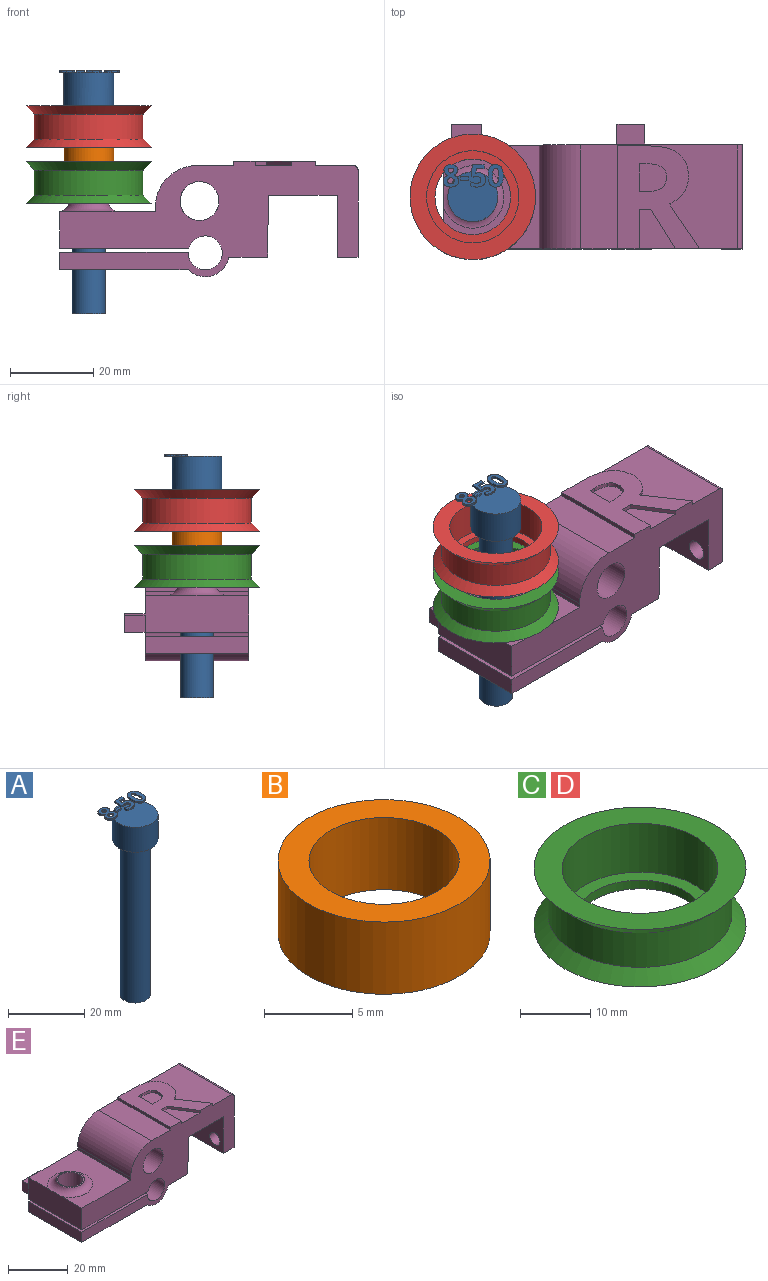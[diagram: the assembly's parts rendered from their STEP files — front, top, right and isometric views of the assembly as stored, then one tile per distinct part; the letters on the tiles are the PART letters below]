
ASSEMBLY  parts=5 mates=4
PART A: 86 faces, bbox 14.5x13.7x58.5 mm
  f0: plane 12x12mm, normal (0,0,1), area 99.4mm2, adj f5,f22,f23,f24,f25,f26,f40,f41
  f1: plane 1x0.26mm, normal (0,0,1), area 0.1mm2, adj f5,f46,f47,f48,f49
  f2: plane 0.85x0.68mm, normal (0,0,1), area 0.2mm2, adj f5,f29,f30,f31
  f3: cylinder r=4mm len=50mm, axis (0,0,-1), area 1256.6mm2, adj f4,f6
  f4: plane 8x8mm, normal (0,0,-1), area 50.3mm2, adj f3
  f5: cylinder r=6mm len=12mm, axis (0,0,-1), area 301.6mm2, adj f0,f1,f2,f6,f39,f45,f67,f85
  f6: plane 12x12mm, normal (0,0,-1), area 62.8mm2, adj f3,f5
  f7: extruded ~0.5x0.46mm, area 0.2mm2, adj f8,f37,f38,f39
  f8: extruded ~0.5x0.46mm, area 0.2mm2, adj f7,f9,f38,f39
  f9: extruded ~0.5x0.39mm, area 0.2mm2, adj f8,f10,f38,f39
  f10: extruded ~0.5x0.4mm, area 0.2mm2, adj f9,f11,f38,f39
  f11: extruded ~0.5x0.49mm, area 0.3mm2, adj f10,f12,f38,f39
  f12: extruded ~0.5x0.5mm, area 0.3mm2, adj f11,f13,f38,f39
  f13: extruded ~0.5x0.39mm, area 0.2mm2, adj f12,f37,f38,f39
  f14: extruded ~1.22x0.5mm, area 0.6mm2, adj f15,f35,f38,f39
  f15: extruded ~1.22x0.5mm, area 0.6mm2, adj f14,f16,f38,f39
  f16: extruded ~0.91x0.5mm, area 0.5mm2, adj f15,f17,f38,f39
  f17: extruded ~0.71x0.5mm, area 0.4mm2, adj f16,f18,f38,f39
  f18: extruded ~0.65x0.61mm, area 0.4mm2, adj f17,f19,f38,f39
  f19: extruded ~0.77x0.62mm, area 0.5mm2, adj f18,f20,f38,f39
  f20: extruded ~0.8x0.5mm, area 0.4mm2, adj f19,f21,f38,f39
  f21: extruded ~1.04x0.5mm, area 0.6mm2, adj f20,f22,f38,f39
  f22: extruded ~1.36x0.5mm, area 0.7mm2, adj f0,f21,f23,f38,f39
  f23: extruded ~1.33x0.5mm, area 0.7mm2, adj f0,f22,f24,f38
  f24: extruded ~1.04x0.51mm, area 0.6mm2, adj f0,f23,f25,f38
  f25: extruded ~0.75x0.5mm, area 0.4mm2, adj f0,f24,f26,f38
  f26: extruded ~0.85x0.66mm, area 0.5mm2, adj f0,f25,f27,f38,f39
  f27: extruded ~0.72x0.56mm, area 0.5mm2, adj f26,f28,f38,f39
  f28: extruded ~0.72x0.5mm, area 0.4mm2, adj f27,f35,f38,f39
  f29: extruded ~0.5x0.45mm, area 0.3mm2, adj f2,f30,f36,f38,f39
  f30: extruded ~0.5x0.47mm, area 0.3mm2, adj f2,f29,f31,f38
  f31: extruded ~0.62x0.5mm, area 0.3mm2, adj f2,f30,f32,f38,f39
  f32: extruded ~0.59x0.5mm, area 0.3mm2, adj f31,f33,f38,f39
  f33: extruded ~0.5x0.48mm, area 0.3mm2, adj f32,f34,f38,f39
  f34: extruded ~0.89x0.77mm, area 0.6mm2, adj f33,f36,f38,f39
  f35: extruded ~0.93x0.5mm, area 0.5mm2, adj f14,f28,f38,f39
  f36: extruded ~0.66x0.5mm, area 0.4mm2, adj f29,f34,f38,f39
  f37: extruded ~0.5x0.39mm, area 0.2mm2, adj f7,f13,f38,f39
  f38: plane 5.4x3.69mm, normal (0,0,1), area 12.7mm2, adj f7,f8,f9,f10,f11,f12,f13,f14
  f39: plane 5.4x3.53mm, normal (0,0,-1), area 10.2mm2, adj f5,f7,f8,f9,f10,f11,f12,f13
  f40: plane 0.9x0.5mm, normal (-1,0,0), area 0.4mm2, adj f0,f41,f43,f44
  f41: plane 1.93x0.5mm, normal (0,-1,0), area 1mm2, adj f0,f40,f42,f44
  f42: plane 0.9x0.5mm, normal (1,0,0), area 0.4mm2, adj f0,f41,f43,f44
  f43: plane 1.93x0.5mm, normal (0,1,0), area 1mm2, adj f0,f40,f42,f44
  f44: plane 1.93x0.9mm, normal (0,0,1), area 1.7mm2, adj f40,f41,f42,f43
  f45: plane 0.76x0.31mm, normal (0,0,-1), area 0mm2, adj f5,f46
  f46: extruded ~1.21x0.5mm, area 0.7mm2, adj f0,f1,f45,f47,f65,f66
  f47: extruded ~0.54x0.5mm, area 0.3mm2, adj f1,f46,f48,f66
  f48: plane 0.5x0.13mm, normal (-0.2,0.98,0), area 0.1mm2, adj f1,f47,f49,f66
  f49: plane 1.03x0.5mm, normal (1,-0.09,0), area 0.5mm2, adj f1,f48,f50,f66,f67
  f50: plane 1.88x0.5mm, normal (0,-1,0), area 0.9mm2, adj f49,f51,f66,f67
  f51: plane 0.94x0.5mm, normal (1,0,0), area 0.5mm2, adj f50,f52,f66,f67
  f52: plane 2.85x0.5mm, normal (0,1,0), area 1.4mm2, adj f51,f53,f66,f67
  f53: plane 2.68x0.5mm, normal (-1,0.07,0), area 1.3mm2, adj f0,f52,f54,f66,f67
  f54: plane 0.5x0.44mm, normal (-0.47,-0.88,0), area 0.3mm2, adj f0,f53,f55,f66
  f55: extruded ~0.5x0.37mm, area 0.2mm2, adj f0,f54,f56,f66
  f56: extruded ~0.5x0.42mm, area 0.2mm2, adj f0,f55,f57,f66
  f57: extruded ~1.05x0.8mm, area 0.8mm2, adj f0,f56,f58,f66
  f58: extruded ~1.02x0.83mm, area 0.8mm2, adj f0,f57,f59,f66
  f59: extruded ~0.72x0.5mm, area 0.4mm2, adj f0,f58,f60,f66
  f60: extruded ~0.66x0.5mm, area 0.4mm2, adj f0,f59,f61,f66
  f61: plane 0.96x0.5mm, normal (-1,0,0), area 0.5mm2, adj f0,f60,f62,f66
  f62: extruded ~1.42x0.5mm, area 0.7mm2, adj f0,f61,f63,f66
  f63: extruded ~1.55x0.5mm, area 0.8mm2, adj f0,f62,f64,f66
  f64: extruded ~1.36x0.54mm, area 0.8mm2, adj f0,f63,f65,f66
  f65: extruded ~1.17x0.5mm, area 0.6mm2, adj f0,f46,f64,f66
  f66: plane 5.33x3.51mm, normal (0,0,1), area 10.9mm2, adj f46,f47,f48,f49,f50,f51,f52,f53
  f67: plane 2.97x1.71mm, normal (0,0,-1), area 3.5mm2, adj f5,f49,f50,f51,f52,f53
  f68: extruded ~1.39x0.5mm, area 0.7mm2, adj f69,f83,f84,f85
  f69: extruded ~1.39x0.5mm, area 0.7mm2, adj f68,f70,f84,f85
  f70: extruded ~0.56x0.5mm, area 0.4mm2, adj f69,f71,f84,f85
  f71: extruded ~0.56x0.5mm, area 0.4mm2, adj f70,f72,f84,f85
  f72: extruded ~1.39x0.5mm, area 0.7mm2, adj f71,f73,f84,f85
  f73: extruded ~1.38x0.5mm, area 0.7mm2, adj f72,f74,f84,f85
  f74: extruded ~0.56x0.5mm, area 0.4mm2, adj f73,f83,f84,f85
  f75: extruded ~2.04x0.5mm, area 1.1mm2, adj f76,f82,f84,f85
  f76: extruded ~2.02x0.5mm, area 1.1mm2, adj f75,f77,f84,f85
  f77: extruded ~1.38x0.69mm, area 0.8mm2, adj f76,f78,f84,f85
  f78: extruded ~1.38x0.66mm, area 0.8mm2, adj f77,f79,f84,f85
  f79: extruded ~2.05x0.5mm, area 1.1mm2, adj f78,f80,f84,f85
  f80: extruded ~2.02x0.5mm, area 1mm2, adj f0,f79,f81,f84,f85
  f81: extruded ~1.37x0.68mm, area 0.8mm2, adj f0,f80,f82,f84
  f82: extruded ~1.39x0.66mm, area 0.8mm2, adj f0,f75,f81,f84,f85
  f83: extruded ~0.56x0.5mm, area 0.4mm2, adj f68,f74,f84,f85
  f84: plane 5.41x3.68mm, normal (0,0,1), area 12.1mm2, adj f68,f69,f70,f71,f72,f73,f74,f75
  f85: plane 5.41x3.68mm, normal (0,0,-1), area 10.3mm2, adj f5,f68,f69,f70,f71,f72,f73,f74
PART B: 4 faces, bbox 12x12x5 mm
  f0: cylinder r=4.25mm len=8.5mm, axis (0,0,-1), area 133.5mm2, adj f2,f3
  f1: cylinder r=6mm len=12mm, axis (0,0,-1), area 188.5mm2, adj f2,f3
  f2: plane 12x12mm, normal (0,0,1), area 56.4mm2, adj f0,f1
  f3: plane 12x12mm, normal (0,0,-1), area 56.4mm2, adj f0,f1
PART C: 8 faces, bbox 30.2x30.2x10 mm
  f0: plane 30.2x30.2mm, normal (0,0,1), area 329.2mm2, adj f1,f7
  f1: cylinder r=11.1mm len=22.2mm, axis (0,0,-1), area 592.8mm2, adj f0,f2
  f2: plane 22.2x22.2mm, normal (0,0,1), area 126.9mm2, adj f1,f3
  f3: cylinder r=9.1mm len=18.2mm, axis (0,0,-1), area 85.8mm2, adj f2,f4
  f4: plane 30.2x30.2mm, normal (0,0,-1), area 456.2mm2, adj f3,f5
  f5: cone r=13.1mm half-angle=45deg, axis (0,0,-1), area 250.6mm2, adj f4,f6
  f6: cylinder r=13.1mm len=26.2mm, axis (0,0,-1), area 493.9mm2, adj f5,f7
  f7: cone r=15.1mm half-angle=45deg, axis (0,0,1), area 250.6mm2, adj f0,f6
PART D: same geometry as C
PART E: 56 faces, bbox 75.2x30x27.7 mm
  f0: plane 37.77x25mm, normal (0,0,1), area 550.8mm2, adj f14,f15,f25,f27,f40,f41,f42,f43
  f1: plane 9.51x8.71mm, normal (0,0,1), area 54.7mm2, adj f14,f37,f38,f39
  f2: plane 25x4.12mm, normal (-1,0,0), area 103mm2, adj f5,f14,f15,f19
  f3: cylinder r=4.17mm len=8.35mm, axis (0,0,1), area 108.1mm2, adj f5,f19
  f4: plane 25x9.34mm, normal (0,0,-1), area 233.4mm2, adj f13,f14,f15,f17
  f5: plane 30.88x25mm, normal (0,0,-1), area 717.2mm2, adj f2,f3,f14,f15,f17
  f6: plane 25x8.82mm, normal (-1,0,0), area 219.6mm2, adj f7,f14,f15,f20,f24
  f7: plane 25x23mm, normal (0,0,1), area 400mm2, adj f6,f8,f14,f15,f24
  f8: plane 25x1.1mm, normal (-1,0,0), area 27.5mm2, adj f7,f14,f15,f25
  f9: plane 25x21.09mm, normal (1,0,0), area 493.5mm2, adj f10,f14,f15,f22,f23,f27
  f10: plane 25x5mm, normal (0,0,-1), area 125mm2, adj f9,f11,f14,f15
  f11: plane 25x15mm, normal (-1,0,0), area 341.3mm2, adj f10,f12,f14,f15,f22,f23
  f12: plane 25x16.55mm, normal (0,0,-1), area 413.8mm2, adj f11,f13,f14,f15
  f13: plane 25x14.91mm, normal (1,0,-0.01), area 372.8mm2, adj f4,f12,f14,f15
  f14: plane 71.77x27.75mm, normal (0,-1,0), area 1042.9mm2, adj f0,f1,f2,f4,f5,f6,f7,f8
  f15: plane 71.77x26.75mm, normal (0,1,0), area 971.8mm2, adj f0,f2,f4,f5,f6,f7,f8,f9
  f16: cylinder r=4.17mm len=10.78mm, axis (0,0,1), area 282.8mm2, adj f20,f21
  f17: cylinder r=5.75mm len=25mm, axis (0,-1,0), area 315.9mm2, adj f4,f5,f14,f15
  f18: cylinder r=4.1mm len=25mm, axis (0,-1,0), area 618.7mm2, adj f14,f15,f19,f20
  f19: plane 30.91x25mm, normal (0,0,1), area 718.1mm2, adj f2,f3,f14,f15,f18
  f20: plane 31.07x30mm, normal (0,0,-1), area 758.4mm2, adj f6,f14,f15,f16,f18,f29,f30,f31
  f21: plane 9.35x9.35mm, normal (0,0,1), area 13.9mm2, adj f16,f24
  f22: cylinder r=2.43mm len=5mm, axis (1,0,0), area 76.2mm2, adj f9,f11
  f23: cylinder r=2.2mm len=5mm, axis (1,0,0), area 69.1mm2, adj f9,f11
  f24: torus R=7.5mm, axis (0,0,-1), area 134.6mm2, adj f6,f7,f21
  f25: cylinder r=10mm len=25mm, axis (0,-1,0), area 392.7mm2, adj f0,f8,f14,f15
  f26: cylinder r=4.68mm len=25mm, axis (0,-1,0), area 735.2mm2, adj f14,f15
  f27: cylinder r=1mm len=25mm, axis (0,-1,0), area 39.3mm2, adj f0,f9,f14,f15
  f28: plane 7.3x5mm, normal (0,0,1), area 36.5mm2, adj f15,f29,f30,f31
  f29: plane 5x4.12mm, normal (-1,0,0), area 20.6mm2, adj f15,f20,f28,f31
  f30: plane 5x4.12mm, normal (1,0,0), area 20.6mm2, adj f15,f20,f28,f31
  f31: plane 7.3x4.12mm, normal (0,1,0), area 30.1mm2, adj f20,f28,f29,f30
  f32: plane 6.63x5mm, normal (0,0,1), area 33.2mm2, adj f15,f33,f35,f36
  f33: plane 5x4.5mm, normal (-1,0,0), area 22.5mm2, adj f15,f32,f34,f36
  f34: plane 6.63x5mm, normal (0,0,-1), area 33.2mm2, adj f15,f33,f35,f36
  f35: plane 5x4.5mm, normal (1,0,0), area 22.5mm2, adj f15,f32,f34,f36
  f36: plane 6.63x4.5mm, normal (0,1,0), area 29.9mm2, adj f32,f33,f34,f35
  f37: plane 9.51x1mm, normal (1,0,0), area 9.5mm2, adj f1,f14,f38,f54
  f38: plane 2.79x1mm, normal (0,-1,0), area 2.8mm2, adj f1,f37,f39,f54
  f39: plane 9.51x5.92mm, normal (-0.85,-0.53,0), area 11.2mm2, adj f1,f14,f38,f54
  f40: extruded ~10.8x7.29mm, area 13mm2, adj f0,f14,f41,f54
  f41: extruded ~3.41x2.67mm, area 4.4mm2, adj f0,f40,f42,f54
  f42: extruded ~3.89x1.2mm, area 4.1mm2, adj f0,f41,f43,f54
  f43: extruded ~5.59x2.42mm, area 6.3mm2, adj f0,f42,f44,f54
  f44: extruded ~7.48x1.84mm, area 7.8mm2, adj f0,f43,f45,f54
  f45: plane 7.22x1mm, normal (0,1,0), area 7.2mm2, adj f0,f44,f46,f54
  f46: plane 24.79x1mm, normal (-1,0,0), area 24.8mm2, adj f0,f14,f45,f54
  f47: plane 1.69x1mm, normal (0,1,0), area 1.7mm2, adj f48,f53,f54,f55
  f48: plane 6.7x1mm, normal (1,0,0), area 6.7mm2, adj f47,f49,f54,f55
  f49: plane 1.6x1mm, normal (0,-1,0), area 1.6mm2, adj f48,f50,f54,f55
  f50: extruded ~3.75x1mm, area 3.9mm2, adj f49,f51,f54,f55
  f51: extruded ~2.51x1.21mm, area 2.9mm2, adj f50,f52,f54,f55
  f52: extruded ~2.61x1.19mm, area 3mm2, adj f51,f53,f54,f55
  f53: extruded ~3.68x1mm, area 3.8mm2, adj f47,f52,f54,f55
  f54: plane 24.79x19.8mm, normal (0,0,1), area 300mm2, adj f14,f37,f38,f39,f40,f41,f42,f43
  f55: plane 6.7x6.56mm, normal (0,0,1), area 38.8mm2, adj f47,f48,f49,f50,f51,f52,f53
PLACE A t=(-103.78,-12.5,-13.6)mm
PLACE B rot(axis=(1,0,0),180deg) t=(-103.78,-12.5,26.4)mm
PLACE C t=(-103.78,-12.5,18.1)mm
PLACE D t=(-103.78,-12.5,31.6)mm
PLACE E at identity
MATE fastened A.f3 <-> D.f1  axis (0,0,-1) through (-103.78,-12.5,36.4)mm
MATE fastened B.f0 <-> C.f1  axis (0,0,1) through (-103.78,-12.5,21.4)mm
MATE fastened C.f1 <-> E.f3  axis (0,0,-1) through (-103.78,-12.5,12.9)mm
MATE fastened D.f1 <-> B.f0  axis (0,0,-1) through (-103.78,-12.5,26.4)mm
